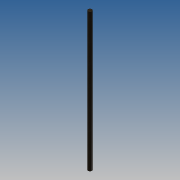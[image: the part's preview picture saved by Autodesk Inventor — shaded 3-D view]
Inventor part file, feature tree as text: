
AUTODESK INVENTOR PART (.ipt)
format: ipt  version: 2014 SP1 (Build 180222100, 222)  size: 127,488 bytes
history: native  units: in
note: dims shown in document units (in); Inventor stores cm internally (conversion verified against a paired STEP export)
features: sketch x8, extrude x6, plane x2
ambient origin geometry x8: Origin, YZ Plane, XZ Plane, XY Plane, X Axis, Y Axis, Z Axis, Center Point
bodies: Solid1 (feature_tree)
feature tree (16):
  extrude  "Extrusion1"  Depth=275.5906in TaperAngle=0.0deg
  extrude  "Extrusion2"  Depth=0.01in TaperAngle=0.0deg
  sketch  "Sketch3"  dims[d7=2.0in d8=3.0in]
  plane  "Work Plane1"
  extrude  "poleStandRadialRef"  Depth=3.0in
  sketch  "Sketch5"  dims[d12=12.0in d13=1.0in d14=0.0in]
  plane  "Work Plane2"
  extrude  "poleStandOffsetRef"  Depth=0.5in
  extrude  "eyeBoltHole"  Depth=1.0in TaperAngle=0.0deg
  extrude  "Extrusion6"  Depth=100.0in
  sketch  "Sketch1"  dims[d0=8.0in d1=275.5906in d2=0.0in]
  sketch  "Sketch2"  dims[d3=39.3701in d4=0.0in d5=0.01in d6=0.0in]
  sketch  "Sketch4"  dims[d9=0.01in d10=0.0in d11=0.5in]
  sketch  "Sketch6"  dims[d15=0.5in d16=100.0in]
  sketch  "Sketch7"  dims[d17=1.0in d18=0.0in]
  sketch  "Sketch8"
